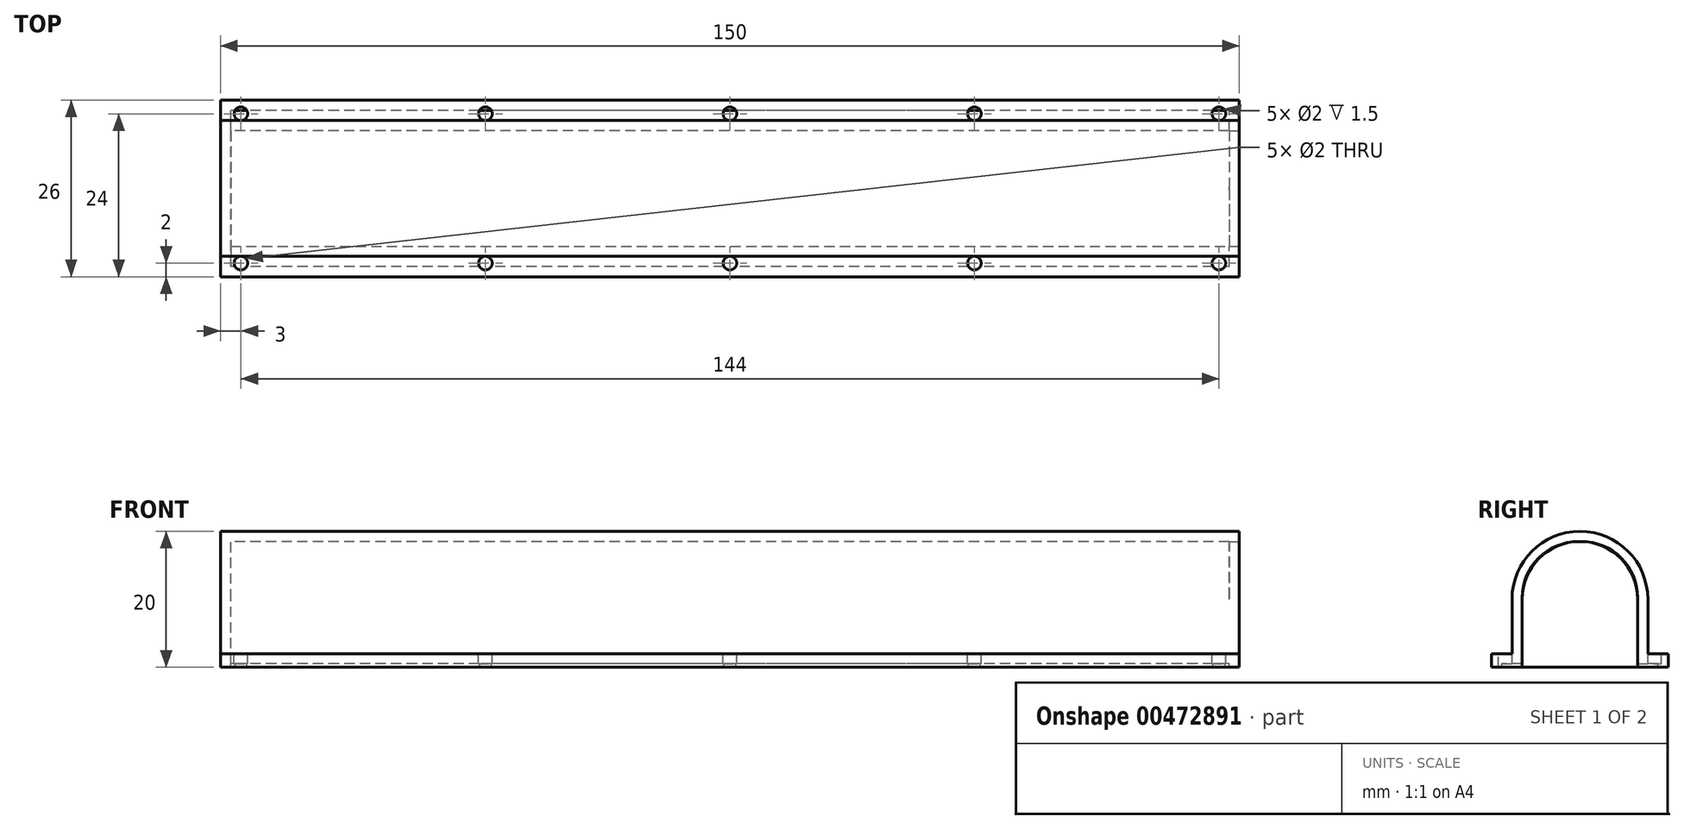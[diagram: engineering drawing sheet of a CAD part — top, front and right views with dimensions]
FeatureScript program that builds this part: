
annotation { "Feature Type Name" : "Feature", "Feature Type Description" : "" }
export const myFeature = defineFeature(function(context is Context, id is Id, definition is map)
    precondition{}
    {
        {
            var Q0;
            Q0=qCreatedBy(makeId("Right.planeOp"),FACE);
            var sketch = newSketch(context, id + "F0", { "sketchPlane" : qUnion([Q0])});
            skLineSegment(sketch, "E0.bottom", {"start": v(-10, 0) * mm, "end": v(10, 0) * mm});
            skLineSegment(sketch, "E0.top", {"start": v(0, 20) * mm, "end": v(0, 20) * mm});
            skLineSegment(sketch, "E0.left", {"start": v(-10, 0) * mm, "end": v(-10, 10) * mm});
            skLineSegment(sketch, "E0.right", {"start": v(10, 0) * mm, "end": v(10, 10) * mm});
            skPoint(sketch, "E1.visualSharp", {"position": v(-10, 20) * mm});
            skArc(sketch, "E1.filletArc", {"start": v(0, 20) * mm, "mid": v(-7.07, 17.07) * mm, "end": v(-10, 10) * mm});
            skPoint(sketch, "E2.visualSharp", {"position": v(10, 20) * mm});
            skArc(sketch, "E2.filletArc", {"start": v(10, 10) * mm, "mid": v(7.07, 17.07) * mm, "end": v(0, 20) * mm});
            skLineSegment(sketch, "E3.bottom", {"start": v(-10, 0) * mm, "end": v(-13, 0) * mm});
            skLineSegment(sketch, "E3.top", {"start": v(-10, 2) * mm, "end": v(-13, 2) * mm});
            skLineSegment(sketch, "E3.left", {"start": v(-10, 0) * mm, "end": v(-10, 2) * mm});
            skLineSegment(sketch, "E3.right", {"start": v(-13, 0) * mm, "end": v(-13, 2) * mm});
            skLineSegment(sketch, "E4.bottom", {"start": v(10, 0) * mm, "end": v(13, 0) * mm});
            skLineSegment(sketch, "E4.top", {"start": v(10, 2) * mm, "end": v(13, 2) * mm});
            skLineSegment(sketch, "E4.left", {"start": v(10, 0) * mm, "end": v(10, 2) * mm});
            skLineSegment(sketch, "E4.right", {"start": v(13, 0) * mm, "end": v(13, 2) * mm});
            skSolve(sketch);
        }
        {
            var Q0;
            Q0=makeQuery(id+"F0.imprint","IMPRINT",FACE,{"disambiguationData":[TD([[makeQuery(id+"F0.imprint","IMPRINT",EDGE,{"derivedFrom":sQuery(id+"F0.wireOp",EDGE,"E0.bottom")}),1.0]])]});
            var Q1;
            Q1=makeQuery(id+"F0.imprint","IMPRINT",FACE,{"disambiguationData":[TD([[makeQuery(id+"F0.imprint","IMPRINT",EDGE,{"derivedFrom":sQuery(id+"F0.wireOp",EDGE,"E3.bottom")}),-1.0]])]});
            var Q2;
            Q2=makeQuery(id+"F0.imprint","IMPRINT",FACE,{"disambiguationData":[TD([[makeQuery(id+"F0.imprint","IMPRINT",EDGE,{"derivedFrom":sQuery(id+"F0.wireOp",EDGE,"E4.bottom")}),1.0]])]});
            extrude(context, id + "F1", {"entities" : qUnion([Q0, Q1, Q2]), "depth" : 150 * mm});
        }
        {
            var Q0;
            Q0=makeQuery(id+"F1.opExtrude","SWEPT_FACE",FACE,{"disambiguationData":[OSD([sQuery(id+"F0.wireOp",EDGE,"E0.bottom"),sQuery(id+"F0.wireOp",EDGE,"E3.bottom"),sQuery(id+"F0.wireOp",EDGE,"E4.bottom")])]});
            shell(context, id + "F2", {"entities" : qUnion([Q0]), "thickness" : 1.5 * mm});
        }
        {
            var Q0;
            Q0=makeQuery(id+"F1.opExtrude","CAP_FACE",FACE,{"disambiguationData":[OSD([sQuery(id+"F0.wireOp",EDGE,"E0.bottom"),sQuery(id+"F0.wireOp",EDGE,"E0.left"),sQuery(id+"F0.wireOp",EDGE,"E0.right"),sQuery(id+"F0.wireOp",EDGE,"E1.filletArc"),sQuery(id+"F0.wireOp",EDGE,"E2.filletArc"),sQuery(id+"F0.wireOp",EDGE,"E3.bottom"),sQuery(id+"F0.wireOp",EDGE,"E3.top"),sQuery(id+"F0.wireOp",EDGE,"E3.right"),sQuery(id+"F0.wireOp",EDGE,"E4.bottom"),sQuery(id+"F0.wireOp",EDGE,"E4.top"),sQuery(id+"F0.wireOp",EDGE,"E4.right")])],"isStart":false});
            var sketch = newSketch(context, id + "F3", { "sketchPlane" : qUnion([Q0])});
            skLineSegment(sketch, "E5.bottom", {"start": v(-8.5, 0) * mm, "end": v(8.5, 0) * mm});
            skLineSegment(sketch, "E5.top", {"start": v(-0.25, 18.5) * mm, "end": v(0.25, 18.5) * mm});
            skLineSegment(sketch, "E5.left", {"start": v(-8.5, 0) * mm, "end": v(-8.5, 10.25) * mm});
            skLineSegment(sketch, "E5.right", {"start": v(8.5, 0) * mm, "end": v(8.5, 10.25) * mm});
            skPoint(sketch, "E6.visualSharp", {"position": v(8.5, 18.5) * mm});
            skArc(sketch, "E6.filletArc", {"start": v(8.5, 10.25) * mm, "mid": v(6.08, 16.08) * mm, "end": v(0.25, 18.5) * mm});
            skPoint(sketch, "E7.visualSharp", {"position": v(-8.5, 18.5) * mm});
            skArc(sketch, "E7.filletArc", {"start": v(-0.25, 18.5) * mm, "mid": v(-6.08, 16.08) * mm, "end": v(-8.5, 10.25) * mm});
            skSolve(sketch);
        }
        {
            var Q0;
            Q0=makeQuery(id+"F3.imprint","IMPRINT",FACE,{"disambiguationData":[TD([[makeQuery(id+"F3.imprint","IMPRINT",EDGE,{"derivedFrom":sQuery(id+"F3.wireOp",EDGE,"E5.bottom")}),1.0]])]});
            extrude(context, id + "F4", {"entities" : qUnion([Q0]), "operationType" : NewBodyOperationType.REMOVE, "oppositeDirection" : true, "depth" : 1.5 * mm});
        }
        {
            var Q0;
            Q0=makeQuery(id+"F1.opExtrude","SWEPT_FACE",FACE,{"disambiguationData":[OSD([sQuery(id+"F0.wireOp",EDGE,"E4.top")])]});
            var sketch = newSketch(context, id + "F5", { "sketchPlane" : qUnion([Q0])});
            skPoint(sketch, "E8.centerSnap0", {"position": v(75, 13) * mm});
            skCircle(sketch, "E9", {"center": v(111, 11) * mm, "radius": 1 * mm});
            skCircle(sketch, "E10", {"center": v(147, 11) * mm, "radius": 1 * mm});
            skCircle(sketch, "E11", {"center": v(75, 11) * mm, "radius": 1 * mm});
            skPoint(sketch, "E11.centerSnap0", {"position": v(75, 10) * mm});
            skCircle(sketch, "E12", {"center": v(39, 11) * mm, "radius": 1 * mm});
            skCircle(sketch, "E13", {"center": v(3, 11) * mm, "radius": 1 * mm});
            skSolve(sketch);
        }
        {
            var Q0;
            Q0=makeQuery(id+"F5.imprint","IMPRINT",FACE,{"disambiguationData":[TD([[makeQuery(id+"F5.imprint","IMPRINT",EDGE,{"derivedFrom":sQuery(id+"F5.wireOp",EDGE,"E13")}),1.0]])]});
            var Q1;
            Q1=makeQuery(id+"F5.imprint","IMPRINT",FACE,{"disambiguationData":[TD([[makeQuery(id+"F5.imprint","IMPRINT",EDGE,{"derivedFrom":sQuery(id+"F5.wireOp",EDGE,"E12")}),1.0]])]});
            var Q2;
            Q2=makeQuery(id+"F5.imprint","IMPRINT",FACE,{"disambiguationData":[TD([[makeQuery(id+"F5.imprint","IMPRINT",EDGE,{"derivedFrom":sQuery(id+"F5.wireOp",EDGE,"E11")}),1.0]])]});
            var Q3;
            Q3=makeQuery(id+"F5.imprint","IMPRINT",FACE,{"disambiguationData":[TD([[makeQuery(id+"F5.imprint","IMPRINT",EDGE,{"derivedFrom":sQuery(id+"F5.wireOp",EDGE,"E9")}),1.0]])]});
            var Q4;
            Q4=makeQuery(id+"F5.imprint","IMPRINT",FACE,{"disambiguationData":[TD([[makeQuery(id+"F5.imprint","IMPRINT",EDGE,{"derivedFrom":sQuery(id+"F5.wireOp",EDGE,"E10")}),1.0]])]});
            extrude(context, id + "F6", {"entities" : qUnion([Q0, Q1, Q2, Q3, Q4]), "operationType" : NewBodyOperationType.REMOVE, "oppositeDirection" : true, "depth" : 1.5 * mm});
        }
        {
            var Q0;
            Q0=makeQuery(id+"F1.opExtrude","SWEPT_FACE",FACE,{"disambiguationData":[OSD([sQuery(id+"F0.wireOp",EDGE,"E3.top")])]});
            var sketch = newSketch(context, id + "F7", { "sketchPlane" : qUnion([Q0])});
            skCircle(sketch, "E14", {"center": v(3, -11) * mm, "radius": 1 * mm});
            skCircle(sketch, "E15", {"center": v(39, -11) * mm, "radius": 1 * mm});
            skCircle(sketch, "E16", {"center": v(75, -11) * mm, "radius": 1 * mm});
            skPoint(sketch, "E16.centerSnap0", {"position": v(75, -10) * mm});
            skCircle(sketch, "E17", {"center": v(111, -11) * mm, "radius": 1 * mm});
            skCircle(sketch, "E18", {"center": v(147, -11) * mm, "radius": 1 * mm});
            skSolve(sketch);
        }
        {
            var Q0;
            Q0=makeQuery(id+"F7.imprint","IMPRINT",FACE,{"disambiguationData":[TD([[makeQuery(id+"F7.imprint","IMPRINT",EDGE,{"derivedFrom":sQuery(id+"F7.wireOp",EDGE,"E18")}),1.0]])]});
            var Q1;
            Q1=makeQuery(id+"F7.imprint","IMPRINT",FACE,{"disambiguationData":[TD([[makeQuery(id+"F7.imprint","IMPRINT",EDGE,{"derivedFrom":sQuery(id+"F7.wireOp",EDGE,"E17")}),1.0]])]});
            var Q2;
            Q2=makeQuery(id+"F7.imprint","IMPRINT",FACE,{"disambiguationData":[TD([[makeQuery(id+"F7.imprint","IMPRINT",EDGE,{"derivedFrom":sQuery(id+"F7.wireOp",EDGE,"E16")}),1.0]])]});
            var Q3;
            Q3=makeQuery(id+"F7.imprint","IMPRINT",FACE,{"disambiguationData":[TD([[makeQuery(id+"F7.imprint","IMPRINT",EDGE,{"derivedFrom":sQuery(id+"F7.wireOp",EDGE,"E15")}),1.0]])]});
            var Q4;
            Q4=makeQuery(id+"F7.imprint","IMPRINT",FACE,{"disambiguationData":[TD([[makeQuery(id+"F7.imprint","IMPRINT",EDGE,{"derivedFrom":sQuery(id+"F7.wireOp",EDGE,"E14")}),1.0]])]});
            extrude(context, id + "F8", {"entities" : qUnion([Q0, Q1, Q2, Q3, Q4]), "operationType" : NewBodyOperationType.REMOVE, "oppositeDirection" : true, "depth" : 2 * mm});
        }
    });
